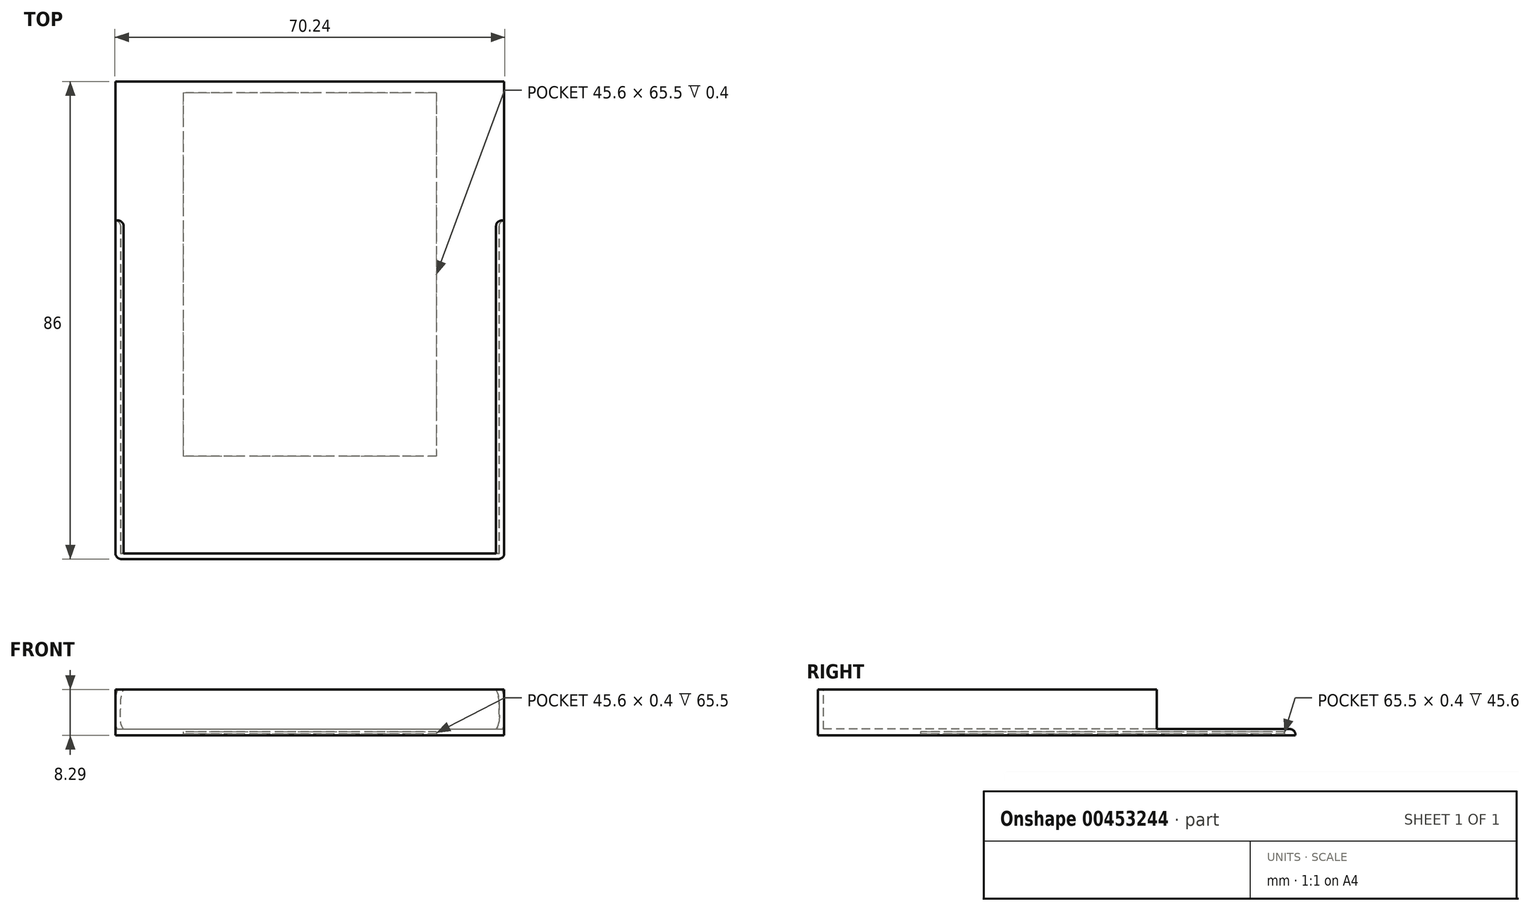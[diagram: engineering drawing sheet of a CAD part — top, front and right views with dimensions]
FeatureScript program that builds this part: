
annotation { "Feature Type Name" : "Feature", "Feature Type Description" : "" }
export const myFeature = defineFeature(function(context is Context, id is Id, definition is map)
    precondition{}
    {
        {
            var Q0;
            Q0=qCreatedBy(makeId("Top.planeOp"),FACE);
            var sketch = newSketch(context, id + "F0", { "sketchPlane" : qUnion([Q0])});
            skLineSegment(sketch, "E0.bottom", {"start": v(0, 0) * mm, "end": v(70, 0) * mm});
            skLineSegment(sketch, "E0.top", {"start": v(0, 85) * mm, "end": v(70, 85) * mm});
            skLineSegment(sketch, "E0.left", {"start": v(0, 0) * mm, "end": v(0, 85) * mm});
            skLineSegment(sketch, "E0.right", {"start": v(70, 0) * mm, "end": v(70, 85) * mm});
            skSolve(sketch);
        }
        {
            var Q0;
            Q0 = qSketchRegion(id + "F0", true);
            extrude(context, id + "F1", {"entities" : qUnion([Q0]), "depth" : .25 * mm});
        }
        {
            var Q0;
            Q0=makeQuery(id+"F1.opExtrude","CAP_FACE",FACE,{"disambiguationData":[OSD([sQuery(id+"F0.wireOp",EDGE,"E0.bottom"),sQuery(id+"F0.wireOp",EDGE,"E0.top"),sQuery(id+"F0.wireOp",EDGE,"E0.left"),sQuery(id+"F0.wireOp",EDGE,"E0.right")])],"isStart":false});
            var sketch = newSketch(context, id + "F2", { "sketchPlane" : qUnion([Q0])});
            skLineSegment(sketch, "E1.0.0", {"start": v(70, 85) * mm, "end": v(0, 85) * mm});
            skLineSegment(sketch, "E1.0.1", {"start": v(0, 85) * mm, "end": v(0, 0) * mm});
            skLineSegment(sketch, "E1.0.2", {"start": v(0, 0) * mm, "end": v(70, 0) * mm});
            skLineSegment(sketch, "E1.0.3", {"start": v(70, 0) * mm, "end": v(70, 85) * mm});
            skLineSegment(sketch, "E2", {"start": v(35, 85) * mm, "end": v(35, 0) * mm, "construction": true});
            skLineSegment(sketch, "E3", {"start": v(35, 83) * mm, "end": v(12.2, 83) * mm});
            skLineSegment(sketch, "E4", {"start": v(12.2, 83) * mm, "end": v(12.2, 17.5) * mm});
            skLineSegment(sketch, "E5", {"start": v(12.2, 17.5) * mm, "end": v(35, 17.5) * mm});
            skLineSegment(sketch, "E6.MirrorCS", {"start": v(35, 83) * mm, "end": v(57.8, 83) * mm});
            skLineSegment(sketch, "E7.MirrorCS", {"start": v(57.8, 83) * mm, "end": v(57.8, 17.5) * mm});
            skLineSegment(sketch, "E8.MirrorCS", {"start": v(57.8, 17.5) * mm, "end": v(35, 17.5) * mm});
            skSolve(sketch);
        }
        {
            var Q0;
            Q0 = qSketchRegion(id + "F2", true);
            extrude(context, id + "F3", {"entities" : qUnion([Q0]), "operationType" : NewBodyOperationType.ADD, "depth" : .4 * mm});
        }
        {
            var Q0;
            Q0=makeQuery(id+"F3.opExtrude","CAP_FACE",FACE,{"disambiguationData":[OSD([sQuery(id+"F2.wireOp",EDGE,"E1.0.0"),sQuery(id+"F2.wireOp",EDGE,"E1.0.1"),sQuery(id+"F2.wireOp",EDGE,"E1.0.2"),sQuery(id+"F2.wireOp",EDGE,"E1.0.3"),sQuery(id+"F2.wireOp",EDGE,"E3"),sQuery(id+"F2.wireOp",EDGE,"E4"),sQuery(id+"F2.wireOp",EDGE,"E5"),sQuery(id+"F2.wireOp",EDGE,"E6.MirrorCS"),sQuery(id+"F2.wireOp",EDGE,"E7.MirrorCS"),sQuery(id+"F2.wireOp",EDGE,"E8.MirrorCS")])],"isStart":false});
            var sketch = newSketch(context, id + "F4", { "sketchPlane" : qUnion([Q0])});
            skLineSegment(sketch, "E9.0.0", {"start": v(70, 85) * mm, "end": v(0, 85) * mm});
            skLineSegment(sketch, "E9.0.1", {"start": v(0, 85) * mm, "end": v(0, 0) * mm});
            skLineSegment(sketch, "E9.0.2", {"start": v(0, 0) * mm, "end": v(70, 0) * mm});
            skLineSegment(sketch, "E9.0.3", {"start": v(70, 0) * mm, "end": v(70, 85) * mm});
            skSolve(sketch);
        }
        {
            var Q0;
            Q0 = qSketchRegion(id + "F4", true);
            extrude(context, id + "F5", {"entities" : qUnion([Q0]), "operationType" : NewBodyOperationType.ADD, "depth" : .5 * mm});
        }
        {
            var Q0;
            Q0=makeQuery(id+"F5.boolean.opBoolean","MERGE",FACE,{"derivedFrom":[makeQuery(id+"F3.boolean.opBoolean","MERGE",FACE,{"derivedFrom":[makeQuery(id+"F1.opExtrude","SWEPT_FACE",FACE,{"disambiguationData":[OSD([sQuery(id+"F0.wireOp",EDGE,"E0.bottom")])]}),makeQuery(id+"F3.opExtrude","SWEPT_FACE",FACE,{"disambiguationData":[OSD([sQuery(id+"F2.wireOp",EDGE,"E1.0.2")])]})]}),makeQuery(id+"F5.opExtrude","SWEPT_FACE",FACE,{"disambiguationData":[OSD([sQuery(id+"F4.wireOp",EDGE,"E9.0.2")])]})]});
            var sketch = newSketch(context, id + "F6", { "sketchPlane" : qUnion([Q0])});
            skLineSegment(sketch, "E10", {"start": v(35, 0) * mm, "end": v(35, 1.15) * mm, "construction": true});
            skLineSegment(sketch, "E11", {"start": v(0, 1.15) * mm, "end": v(0, 8.29) * mm});
            skLineSegment(sketch, "E12", {"start": v(0, 8.29) * mm, "end": v(1.47, 8.29) * mm});
            skFitSpline(sketch, "E13", {"points": [v(1.45, 1.15) * mm, v(0.92, 4.86) * mm, v(1.47, 8.29) * mm], "startDerivative": vector(-4.48, 4.8) * mm, "endDerivative": vector(4.03, 9.1) * mm});
            skLineSegment(sketch, "E14.MirrorCS", {"start": v(70, 8.29) * mm, "end": v(68.53, 8.29) * mm});
            skLineSegment(sketch, "E15.MirrorCS", {"start": v(70, 1.15) * mm, "end": v(70, 8.29) * mm});
            skFitSpline(sketch, "E16.MirrorCS", {"points": [v(68.55, 1.15) * mm, v(69.08, 4.86) * mm, v(68.53, 8.29) * mm], "startDerivative": vector(4.48, 4.8) * mm, "endDerivative": vector(-4.03, 9.1) * mm});
            skLineSegment(sketch, "E17", {"start": v(0, 1.15) * mm, "end": v(1.45, 1.15) * mm});
            skLineSegment(sketch, "E18.MirrorCS", {"start": v(70, 1.15) * mm, "end": v(68.55, 1.15) * mm});
            skSolve(sketch);
        }
        {
            var Q0;
            Q0 = qSketchRegion(id + "F6", true);
            var Q1;
            Q1=makeQuery(id+"F5.boolean.opBoolean","MERGE",FACE,{"derivedFrom":[makeQuery(id+"F3.boolean.opBoolean","MERGE",FACE,{"derivedFrom":[makeQuery(id+"F1.opExtrude","SWEPT_FACE",FACE,{"disambiguationData":[OSD([sQuery(id+"F0.wireOp",EDGE,"E0.top")])]}),makeQuery(id+"F3.opExtrude","SWEPT_FACE",FACE,{"disambiguationData":[OSD([sQuery(id+"F2.wireOp",EDGE,"E1.0.0")])]})]}),makeQuery(id+"F5.opExtrude","SWEPT_FACE",FACE,{"disambiguationData":[OSD([sQuery(id+"F4.wireOp",EDGE,"E9.0.0")])]})]});
            extrude(context, id + "F7", {"entities" : qUnion([Q0]), "operationType" : NewBodyOperationType.ADD, "oppositeDirection" : true, "endBoundEntityFace" : qUnion([Q1]), "depth" : 60 * mm});
        }
        {
            var Q0;
            Q0=makeQuery(id+"F7.boolean.opBoolean","MERGE",FACE,{"derivedFrom":[makeQuery(id+"F5.boolean.opBoolean","MERGE",FACE,{"derivedFrom":[makeQuery(id+"F3.boolean.opBoolean","MERGE",FACE,{"derivedFrom":[makeQuery(id+"F1.opExtrude","SWEPT_FACE",FACE,{"disambiguationData":[OSD([sQuery(id+"F0.wireOp",EDGE,"E0.bottom")])]}),makeQuery(id+"F3.opExtrude","SWEPT_FACE",FACE,{"disambiguationData":[OSD([sQuery(id+"F2.wireOp",EDGE,"E1.0.2")])]})]}),makeQuery(id+"F5.opExtrude","SWEPT_FACE",FACE,{"disambiguationData":[OSD([sQuery(id+"F4.wireOp",EDGE,"E9.0.2")])]})]}),makeQuery(id+"F7.opExtrude","CAP_FACE",FACE,{"disambiguationData":[OSD([sQuery(id+"F6.wireOp",EDGE,"E11"),sQuery(id+"F6.wireOp",EDGE,"E12"),sQuery(id+"F6.wireOp",EDGE,"E13"),sQuery(id+"F6.wireOp",EDGE,"E17")])],"isStart":true}),makeQuery(id+"F7.opExtrude","CAP_FACE",FACE,{"disambiguationData":[OSD([sQuery(id+"F6.wireOp",EDGE,"E14.MirrorCS"),sQuery(id+"F6.wireOp",EDGE,"E15.MirrorCS"),sQuery(id+"F6.wireOp",EDGE,"E16.MirrorCS"),sQuery(id+"F6.wireOp",EDGE,"E18.MirrorCS")])],"isStart":true})]});
            var sketch = newSketch(context, id + "F8", { "sketchPlane" : qUnion([Q0])});
            skLineSegment(sketch, "E19.bottom", {"start": v(0, 8.29) * mm, "end": v(70, 8.29) * mm});
            skLineSegment(sketch, "E19.top", {"start": v(0, 0) * mm, "end": v(70, 0) * mm});
            skLineSegment(sketch, "E19.left", {"start": v(0, 8.29) * mm, "end": v(0, 0) * mm});
            skLineSegment(sketch, "E19.right", {"start": v(70, 8.29) * mm, "end": v(70, 0) * mm});
            skSolve(sketch);
        }
        {
            var Q0;
            Q0 = qSketchRegion(id + "F8", true);
            extrude(context, id + "F9", {"entities" : qUnion([Q0]), "operationType" : NewBodyOperationType.ADD, "depth" : 1 * mm});
        }
        {
            var Q0;
            Q0=makeQuery(id+"F7.opExtrude","CAP_EDGE",EDGE,{"disambiguationData":[OSD([sQuery(id+"F6.wireOp",EDGE,"E16.MirrorCS")])],"isStart":true});
            var Q1;
            Q1=makeQuery(id+"F7.opExtrude","CAP_EDGE",EDGE,{"disambiguationData":[OSD([sQuery(id+"F6.wireOp",EDGE,"E13")])],"isStart":true});
            var Q2;
            Q2=makeQuery(id+"F9.opExtrude","CAP_EDGE",EDGE,{"disambiguationData":[OSD([sQuery(id+"F8.wireOp",EDGE,"E19.right")])],"isStart":false});
            var Q3;
            Q3=makeQuery(id+"F9.opExtrude","CAP_EDGE",EDGE,{"disambiguationData":[OSD([sQuery(id+"F8.wireOp",EDGE,"E19.left")])],"isStart":false});
            var Q4;
            Q4=makeQuery(id+"F7.opExtrude","CAP_EDGE",EDGE,{"disambiguationData":[OSD([sQuery(id+"F6.wireOp",EDGE,"E16.MirrorCS")])],"isStart":false});
            var Q5;
            Q5=makeQuery(id+"F7.opExtrude","CAP_EDGE",EDGE,{"disambiguationData":[OSD([sQuery(id+"F6.wireOp",EDGE,"E13")])],"isStart":false});
            var Q6;
            Q6=makeQuery(id+"F5.opExtrude","CAP_EDGE",EDGE,{"disambiguationData":[OSD([sQuery(id+"F4.wireOp",EDGE,"E9.0.0")])],"isStart":false});
            fillet(context, id + "F10", {"entities" : qUnion([Q0, Q1, Q2, Q3, Q4, Q5, Q6]), "radius" : 1 * mm, "tangentPropagation" : true, "allowEdgeOverflow" : false});
        }
    });
